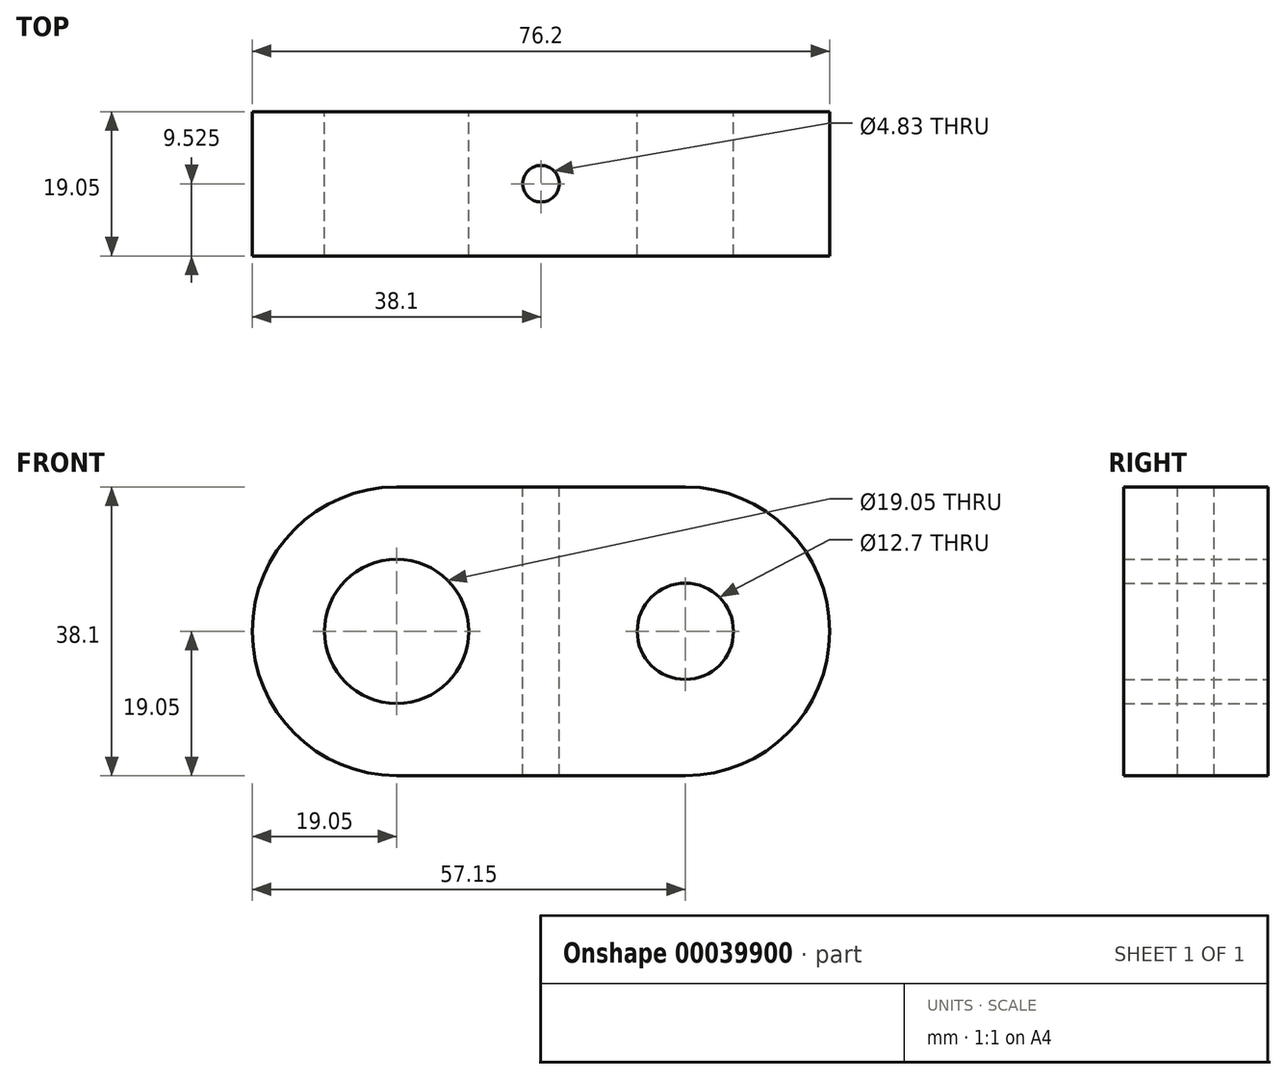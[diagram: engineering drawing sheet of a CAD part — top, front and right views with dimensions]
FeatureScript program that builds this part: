
annotation { "Feature Type Name" : "Feature", "Feature Type Description" : "" }
export const myFeature = defineFeature(function(context is Context, id is Id, definition is map)
    precondition{}
    {
        {
            var Q0;
            Q0=qCreatedBy(makeId("Front.planeOp"),FACE);
            var sketch = newSketch(context, id + "F0", { "sketchPlane" : qUnion([Q0])});
            skLineSegment(sketch, "E0.rect.bottom", {"start": v(19.05, 19.05) * mm, "end": v(-19.05, 19.05) * mm});
            skLineSegment(sketch, "E0.rect.top", {"start": v(19.05, -19.05) * mm, "end": v(-19.05, -19.05) * mm});
            skLineSegment(sketch, "E0.rect.left", {"start": v(38.1, 0) * mm, "end": v(38.1, 0) * mm});
            skLineSegment(sketch, "E0.rect.right", {"start": v(-38.1, 0) * mm, "end": v(-38.1, 0) * mm});
            skPoint(sketch, "E0.rect.middle", {"position": v(0, 0) * mm});
            skPoint(sketch, "E1.visualSharp", {"position": v(-38.1, 19.05) * mm});
            skArc(sketch, "E1.filletArc", {"start": v(-19.05, 19.05) * mm, "mid": v(-32.52, 13.47) * mm, "end": v(-38.1, 0) * mm});
            skPoint(sketch, "E2.visualSharp", {"position": v(-38.1, -19.05) * mm});
            skArc(sketch, "E2.filletArc", {"start": v(-38.1, 0) * mm, "mid": v(-32.52, -13.47) * mm, "end": v(-19.05, -19.05) * mm});
            skPoint(sketch, "E3.visualSharp", {"position": v(38.1, -19.05) * mm});
            skArc(sketch, "E3.filletArc", {"start": v(19.05, -19.05) * mm, "mid": v(32.52, -13.47) * mm, "end": v(38.1, 0) * mm});
            skPoint(sketch, "E4.visualSharp", {"position": v(38.1, 19.05) * mm});
            skArc(sketch, "E4.filletArc", {"start": v(38.1, 0) * mm, "mid": v(32.52, 13.47) * mm, "end": v(19.05, 19.05) * mm});
            skCircle(sketch, "E5", {"center": v(-19.05, 0) * mm, "radius": 9.53 * mm});
            skCircle(sketch, "E6", {"center": v(19.05, 0) * mm, "radius": 6.35 * mm});
            skSolve(sketch);
        }
        {
            var Q0;
            Q0=makeQuery(id+"F0.imprint","IMPRINT",FACE,{"disambiguationData":[TD([[makeQuery(id+"F0.imprint","IMPRINT",EDGE,{"derivedFrom":sQuery(id+"F0.wireOp",EDGE,"E0.rect.bottom")}),1.0]])]});
            extrude(context, id + "F1", {"entities" : qUnion([Q0]), "depth" : 19.05 * mm});
        }
        {
            var Q0;
            Q0=makeQuery(id+"F1.opExtrude","SWEPT_FACE",FACE,{"disambiguationData":[OSD([sQuery(id+"F0.wireOp",EDGE,"E0.rect.bottom")])]});
            var sketch = newSketch(context, id + "F2", { "sketchPlane" : qUnion([Q0])});
            skLineSegment(sketch, "E7", {"start": v(-38.1, -19.05) * mm, "end": v(-38.1, 0) * mm});
            skLineSegment(sketch, "E8", {"start": v(38.1, 0) * mm, "end": v(38.1, -19.05) * mm});
            skCircle(sketch, "E9", {"center": v(0, -9.52) * mm, "radius": 2.41 * mm});
            skSolve(sketch);
        }
        {
            var Q0;
            Q0=makeQuery(id+"F2.imprint","IMPRINT",FACE,{"disambiguationData":[TD([[makeQuery(id+"F2.imprint","IMPRINT",EDGE,{"derivedFrom":sQuery(id+"F2.wireOp",EDGE,"E9")}),1.0]])]});
            extrude(context, id + "F3", {"entities" : qUnion([Q0]), "operationType" : NewBodyOperationType.REMOVE, "oppositeDirection" : true, "depth" : 38.1 * mm});
        }
    });
